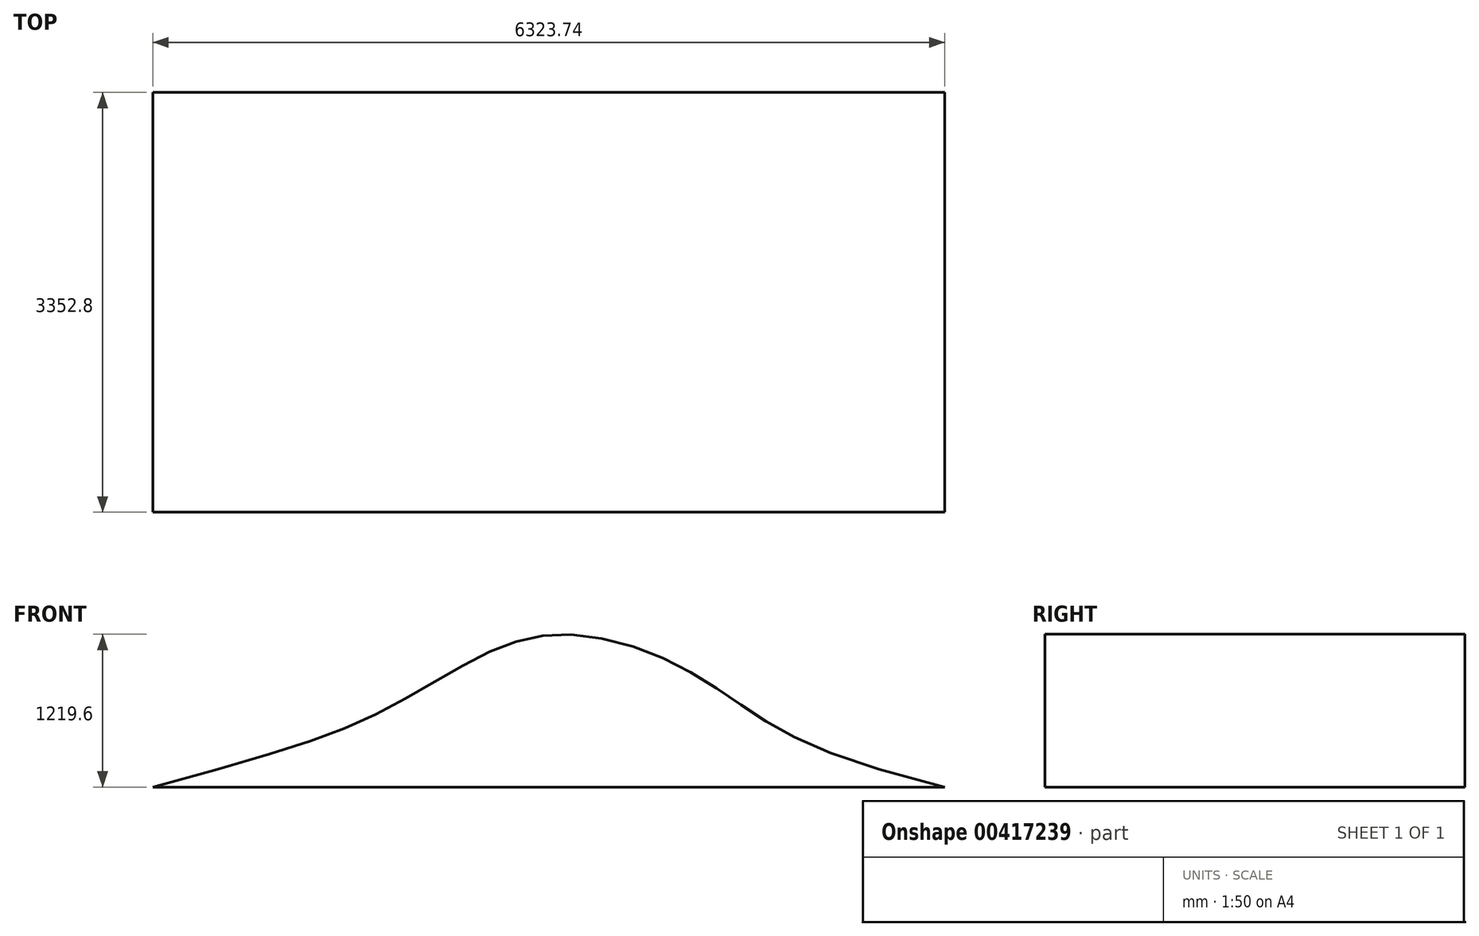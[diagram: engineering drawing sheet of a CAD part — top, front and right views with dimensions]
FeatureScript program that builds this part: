
annotation { "Feature Type Name" : "Feature", "Feature Type Description" : "" }
export const myFeature = defineFeature(function(context is Context, id is Id, definition is map)
    precondition{}
    {
        {
            var Q0;
            Q0=qCreatedBy(makeId("Front.planeOp"),FACE);
            var sketch = newSketch(context, id + "F0", { "sketchPlane" : qUnion([Q0])});
            skFitSpline(sketch, "E0", {"points": [v(0, 0) * mm, v(1786.6, 584) * mm, v(2603.3, 1037.71) * mm, v(3238.5, 1219.2) * mm, v(4055.18, 1037.71) * mm, v(4735.75, 629.37) * mm, v(6323.74, 0) * mm], "startDerivative": vector(13341.44, 3664.39) * mm, "endDerivative": vector(13866.67, -3377.63) * mm});
            skLineSegment(sketch, "E1", {"start": v(0, 0) * mm, "end": v(6323.74, 0) * mm});
            skSolve(sketch);
        }
        {
            var Q0;
            Q0=makeQuery(id+"F0.imprint","IMPRINT",FACE,{"disambiguationData":[TD([[makeQuery(id+"F0.imprint","IMPRINT",EDGE,{"derivedFrom":sQuery(id+"F0.wireOp",EDGE,"E0")}),-1.0]])]});
            extrude(context, id + "F1", {"entities" : qUnion([Q0]), "depth" : 3352.8 * mm});
        }
    });
